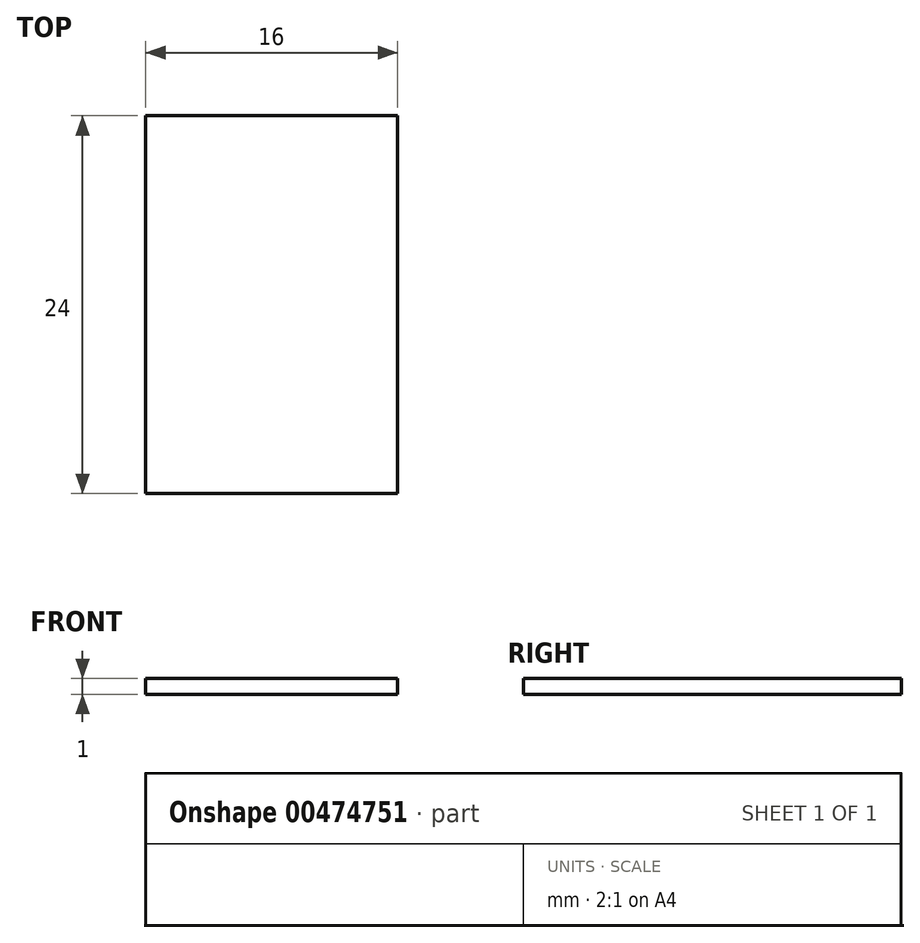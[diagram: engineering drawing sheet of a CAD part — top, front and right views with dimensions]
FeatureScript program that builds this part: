
annotation { "Feature Type Name" : "Feature", "Feature Type Description" : "" }
export const myFeature = defineFeature(function(context is Context, id is Id, definition is map)
    precondition{}
    {
        {
            var Q0;
            Q0=qCreatedBy(makeId("Top.planeOp"),FACE);
            var sketch = newSketch(context, id + "F0", { "sketchPlane" : qUnion([Q0])});
            skLineSegment(sketch, "E0.bottom", {"start": v(0, 0) * mm, "end": v(16, 0) * mm});
            skLineSegment(sketch, "E0.top", {"start": v(0, 24) * mm, "end": v(16, 24) * mm});
            skLineSegment(sketch, "E0.left", {"start": v(0, 0) * mm, "end": v(0, 24) * mm});
            skLineSegment(sketch, "E0.right", {"start": v(16, 0) * mm, "end": v(16, 24) * mm});
            skSolve(sketch);
        }
        {
            var Q0;
            Q0 = qSketchRegion(id + "F0", true);
            extrude(context, id + "F1", {"entities" : qUnion([Q0]), "depth" : 1 * mm});
        }
    });
